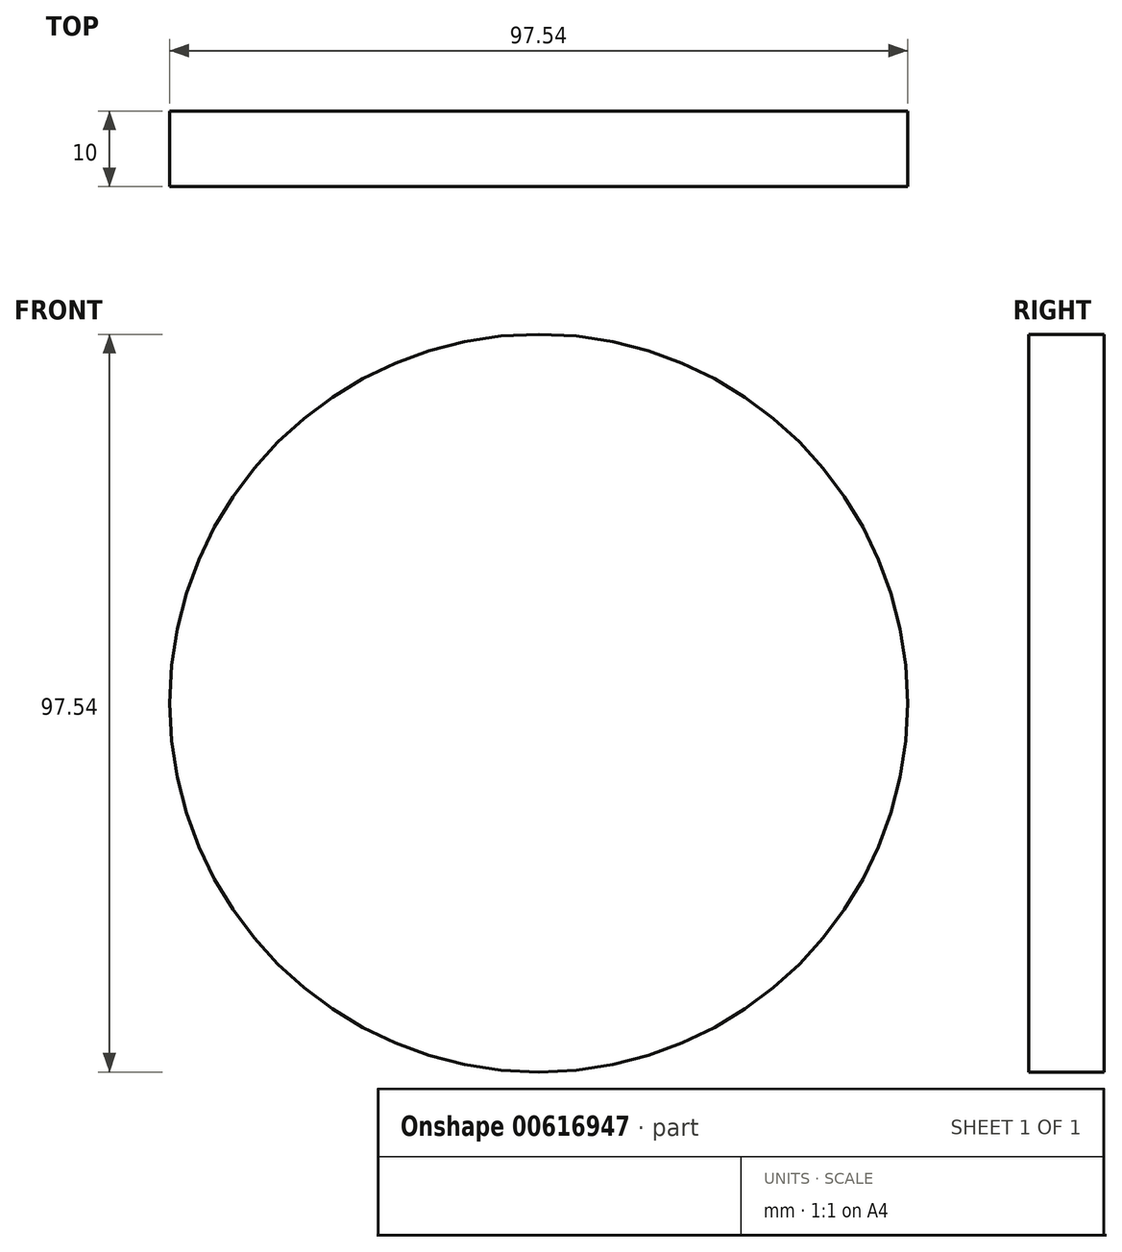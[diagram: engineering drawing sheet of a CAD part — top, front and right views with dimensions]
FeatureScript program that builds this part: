
annotation { "Feature Type Name" : "Feature", "Feature Type Description" : "" }
export const myFeature = defineFeature(function(context is Context, id is Id, definition is map)
    precondition{}
    {
        {
            var Q0;
            Q0=qCreatedBy(makeId("Front.planeOp"),FACE);
            var sketch = newSketch(context, id + "F0", { "sketchPlane" : qUnion([Q0])});
            skCircle(sketch, "E0", {"center": v(0, 0) * mm, "radius": 48.77 * mm});
            skSolve(sketch);
        }
        {
            var Q0;
            Q0=makeQuery(id+"F0.imprint","IMPRINT",FACE,{"disambiguationData":[TD([[makeQuery(id+"F0.imprint","IMPRINT",EDGE,{"derivedFrom":sQuery(id+"F0.wireOp",EDGE,"E0")}),1.0]])]});
            extrude(context, id + "F1", {"entities" : qUnion([Q0]), "depth" : 10 * mm, "offsetDistance" : 25.4 * mm});
        }
    });
